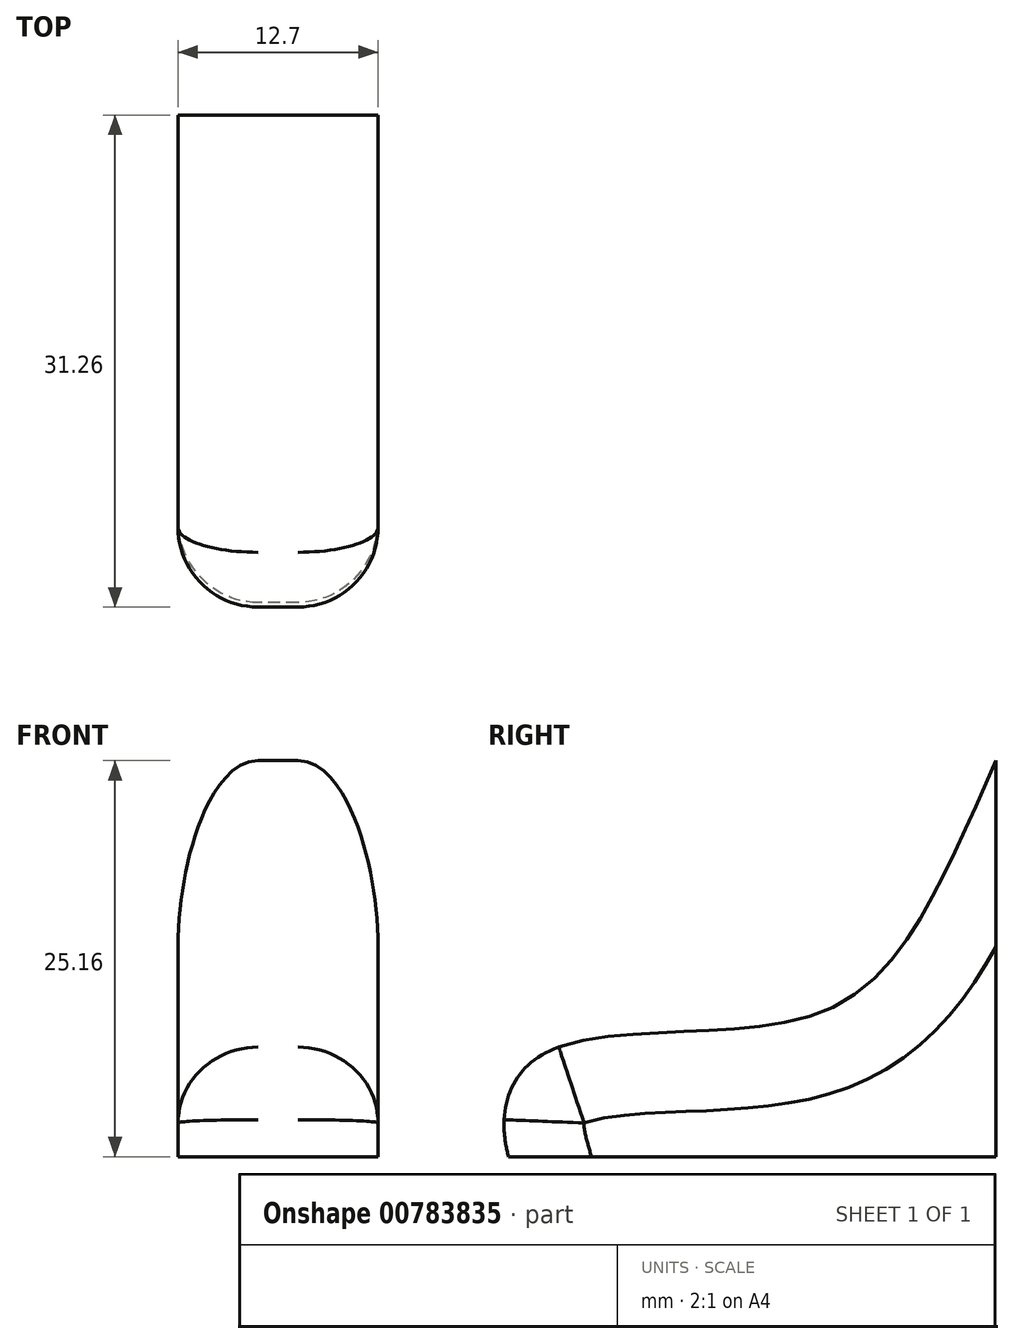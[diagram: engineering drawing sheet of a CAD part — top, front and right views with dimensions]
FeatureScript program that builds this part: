
annotation { "Feature Type Name" : "Feature", "Feature Type Description" : "" }
export const myFeature = defineFeature(function(context is Context, id is Id, definition is map)
    precondition{}
    {
        {
            var Q0;
            Q0=qCreatedBy(makeId("Right.planeOp"),FACE);
            var sketch = newSketch(context, id + "F0", { "sketchPlane" : qUnion([Q0])});
            skFitSpline(sketch, "E0", {"points": [v(-26.71, 0) * mm, v(-24.4, 6.58) * mm, v(-7.61, 8.9) * mm, v(0, 16.13) * mm, v(4.26, 25.16) * mm], "startDerivative": vector(-10.88, 40.31) * mm, "endDerivative": vector(16.63, 37.66) * mm});
            skLineSegment(sketch, "E1", {"start": v(4.26, 25.16) * mm, "end": v(4.26, 0) * mm});
            skLineSegment(sketch, "E2", {"start": v(4.26, 0) * mm, "end": v(-26.71, 0) * mm});
            skSolve(sketch);
        }
        {
            var Q0;
            Q0=makeQuery(id+"F0.imprint","IMPRINT",FACE,{"disambiguationData":[TD([[makeQuery(id+"F0.imprint","IMPRINT",EDGE,{"derivedFrom":sQuery(id+"F0.wireOp",EDGE,"E0")}),-1.0]])]});
            extrude(context, id + "F1", {"entities" : qUnion([Q0]), "depth" : 12.7 * mm, "offsetDistance" : 25.4 * mm});
        }
        {
            var Q0;
            Q0=makeQuery(id+"F1.opExtrude","CAP_EDGE",EDGE,{"disambiguationData":[OSD([sQuery(id+"F0.wireOp",EDGE,"E0")])],"isStart":true});
            var Q1;
            Q1=makeQuery(id+"F1.opExtrude","CAP_EDGE",EDGE,{"disambiguationData":[OSD([sQuery(id+"F0.wireOp",EDGE,"E0")])],"isStart":false});
            fillet(context, id + "F2", {"entities" : qUnion([Q0, Q1]), "radius" : 5.08 * mm, "tangentPropagation" : true, "allowEdgeOverflow" : false});
        }
    });
